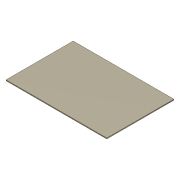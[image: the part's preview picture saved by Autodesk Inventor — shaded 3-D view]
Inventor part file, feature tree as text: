
AUTODESK INVENTOR PART (.ipt)
format: ipt  version: 2012 (Build 160160000, 160)  size: 71,680 bytes
history: native  units: in
note: dims shown in document units (in); Inventor stores cm internally (conversion verified against a paired STEP export)
features: extrude x1, sketch x1
ambient origin geometry x8: Origin, YZ Plane, XZ Plane, XY Plane, X Axis, Y Axis, Z Axis, Center Point
bodies: Solid1 (feature_tree)
feature tree (2):
  extrude  "Extrusion1"  Depth=18.0in
  sketch  "Sketch1"  dims[d0=27.0in d1=18.0in d2=0.25in d3=0.0in]
